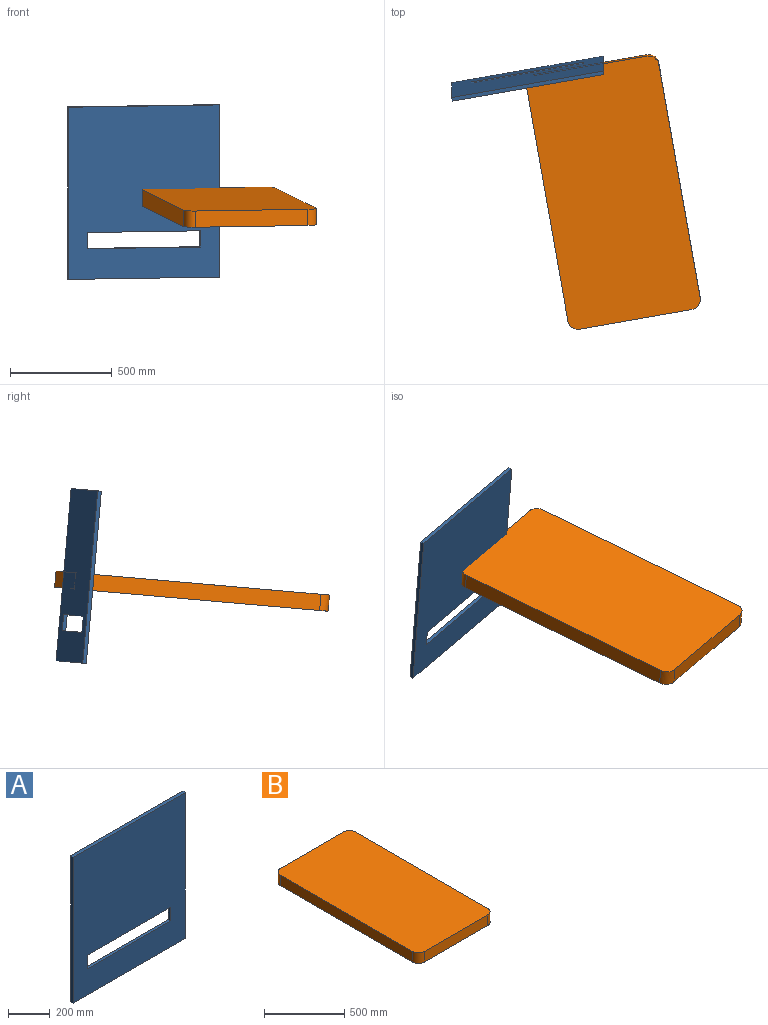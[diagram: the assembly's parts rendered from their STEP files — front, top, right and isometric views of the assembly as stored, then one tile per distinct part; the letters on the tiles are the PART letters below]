
ASSEMBLY  parts=2 mates=1
PART A: 10 faces, bbox 755.8x18x850 mm
  f0: plane 755.78x18mm, normal (0,0,1), area 13604.1mm2, adj f1,f7,f8,f9
  f1: plane 850x18mm, normal (-1,0,0), area 15300mm2, adj f0,f2,f8,f9
  f2: plane 755.78x18mm, normal (0,0,-1), area 13604.1mm2, adj f1,f7,f8,f9
  f3: plane 80x18mm, normal (1,0,0), area 1440mm2, adj f4,f6,f8,f9
  f4: plane 560x18mm, normal (0,0,-1), area 10080mm2, adj f3,f5,f8,f9
  f5: plane 80x18mm, normal (-1,0,0), area 1440mm2, adj f4,f6,f8,f9
  f6: plane 560x18mm, normal (0,0,1), area 10080mm2, adj f3,f5,f8,f9
  f7: plane 850x18mm, normal (1,0,0), area 15300mm2, adj f0,f2,f8,f9
  f8: plane 850x755.78mm, normal (0,-1,0), area 597616.5mm2, adj f0,f1,f2,f3,f4,f5,f6,f7
  f9: plane 850x755.78mm, normal (0,1,0), area 597616.5mm2, adj f0,f1,f2,f3,f4,f5,f6,f7
PART B: 10 faces, bbox 660x1270x80 mm
  f0: plane 560x80mm, normal (0,1,0), area 44800mm2, adj f4,f5,f6,f9
  f1: plane 1170x80mm, normal (-1,0,0), area 93600mm2, adj f4,f5,f6,f7
  f2: plane 560x80mm, normal (0,-1,0), area 44800mm2, adj f4,f5,f7,f8
  f3: plane 1170x80mm, normal (1,0,0), area 93600mm2, adj f4,f5,f8,f9
  f4: plane 1270x660mm, normal (0,0,1), area 836054mm2, adj f0,f1,f2,f3,f6,f7,f8,f9
  f5: plane 1270x660mm, normal (0,0,-1), area 836054mm2, adj f0,f1,f2,f3,f6,f7,f8,f9
  f6: cylinder r=50mm len=80mm, axis (0,0,1), area 6283.2mm2, adj f0,f1,f4,f5
  f7: cylinder r=50mm len=80mm, axis (0,0,-1), area 6283.2mm2, adj f1,f2,f4,f5
  f8: cylinder r=50mm len=80mm, axis (0,0,1), area 6283.2mm2, adj f2,f3,f4,f5
  f9: cylinder r=50mm len=80mm, axis (0,0,-1), area 6283.2mm2, adj f0,f3,f4,f5
PLACE A rot(axis=(0.45,-0.04,0.89),11.2deg) t=(-644.98,786.88,-44.47)mm
PLACE B rot(axis=(0.45,-0.04,0.89),11.2deg) t=(-204.41,-602.89,133.82)mm fixed
MATE planar B.f0 <-> A.f9  axis (-0.17,0.98,0.09) through (-355.42,175.35,242.06)mm
